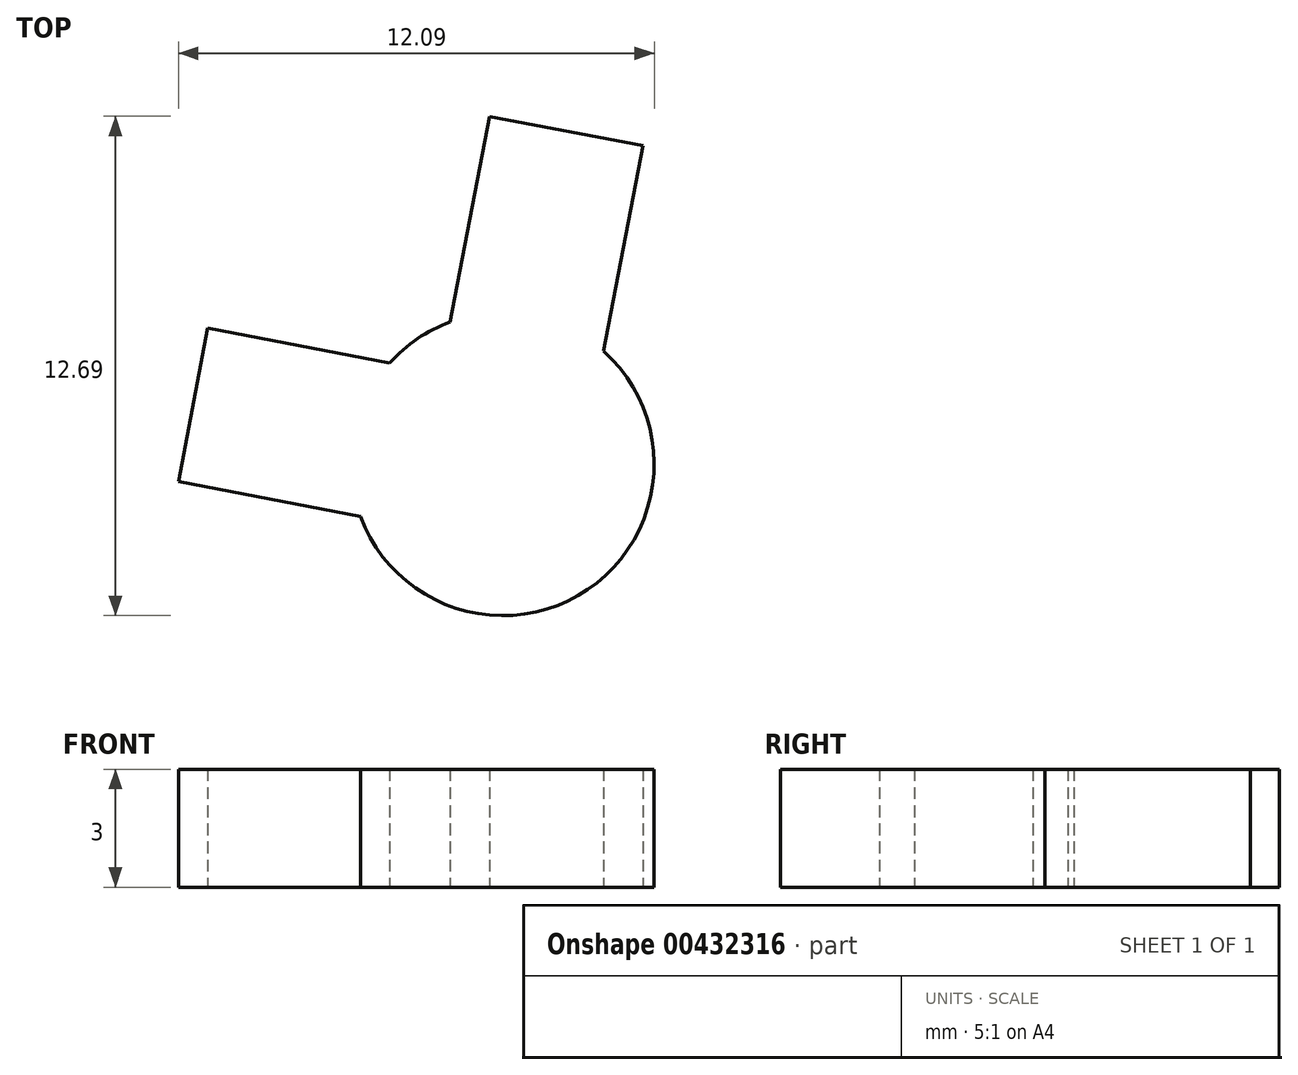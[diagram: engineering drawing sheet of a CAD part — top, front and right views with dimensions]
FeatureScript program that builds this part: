
annotation { "Feature Type Name" : "Feature", "Feature Type Description" : "" }
export const myFeature = defineFeature(function(context is Context, id is Id, definition is map)
    precondition{}
    {
        {
            var Q0;
            Q0=qCreatedBy(makeId("Top.planeOp"),FACE);
            var sketch = newSketch(context, id + "F0", { "sketchPlane" : qUnion([Q0])});
            skArc(sketch, "E0", {"start": v(2.65, -6.14) * mm, "mid": v(8.43, -8) * mm, "end": v(8.83, -1.94) * mm});
            skLineSegment(sketch, "E1", {"start": v(6.27, -4.8) * mm, "end": v(7.88, 3.65) * mm, "construction": true});
            skLineSegment(sketch, "E2", {"start": v(6.27, -4.8) * mm, "end": v(-1.6, -3.3) * mm, "construction": true});
            skLineSegment(sketch, "E3", {"start": v(5.93, 4.03) * mm, "end": v(9.83, 3.28) * mm});
            skLineSegment(sketch, "E4", {"start": v(-1.97, -5.26) * mm, "end": v(-1.23, -1.36) * mm});
            skLineSegment(sketch, "E5", {"start": v(5.93, 4.03) * mm, "end": v(4.94, -1.2) * mm});
            skLineSegment(sketch, "E6", {"start": v(9.83, 3.28) * mm, "end": v(8.83, -1.94) * mm});
            skLineSegment(sketch, "E7", {"start": v(-1.23, -1.36) * mm, "end": v(3.4, -2.24) * mm});
            skLineSegment(sketch, "E8", {"start": v(-1.97, -5.26) * mm, "end": v(2.65, -6.14) * mm});
            skArc(sketch, "E9.trimOffspring", {"start": v(4.94, -1.2) * mm, "mid": v(4.1, -1.62) * mm, "end": v(3.4, -2.24) * mm});
            skSolve(sketch);
        }
        {
            var Q0;
            Q0=makeQuery(id+"F0.imprint","IMPRINT",FACE,{"disambiguationData":[TD([[makeQuery(id+"F0.imprint","IMPRINT",EDGE,{"derivedFrom":sQuery(id+"F0.wireOp",EDGE,"E0")}),1.0]])]});
            extrude(context, id + "F1", {"entities" : qUnion([Q0]), "depth" : 3 * mm});
        }
    });
